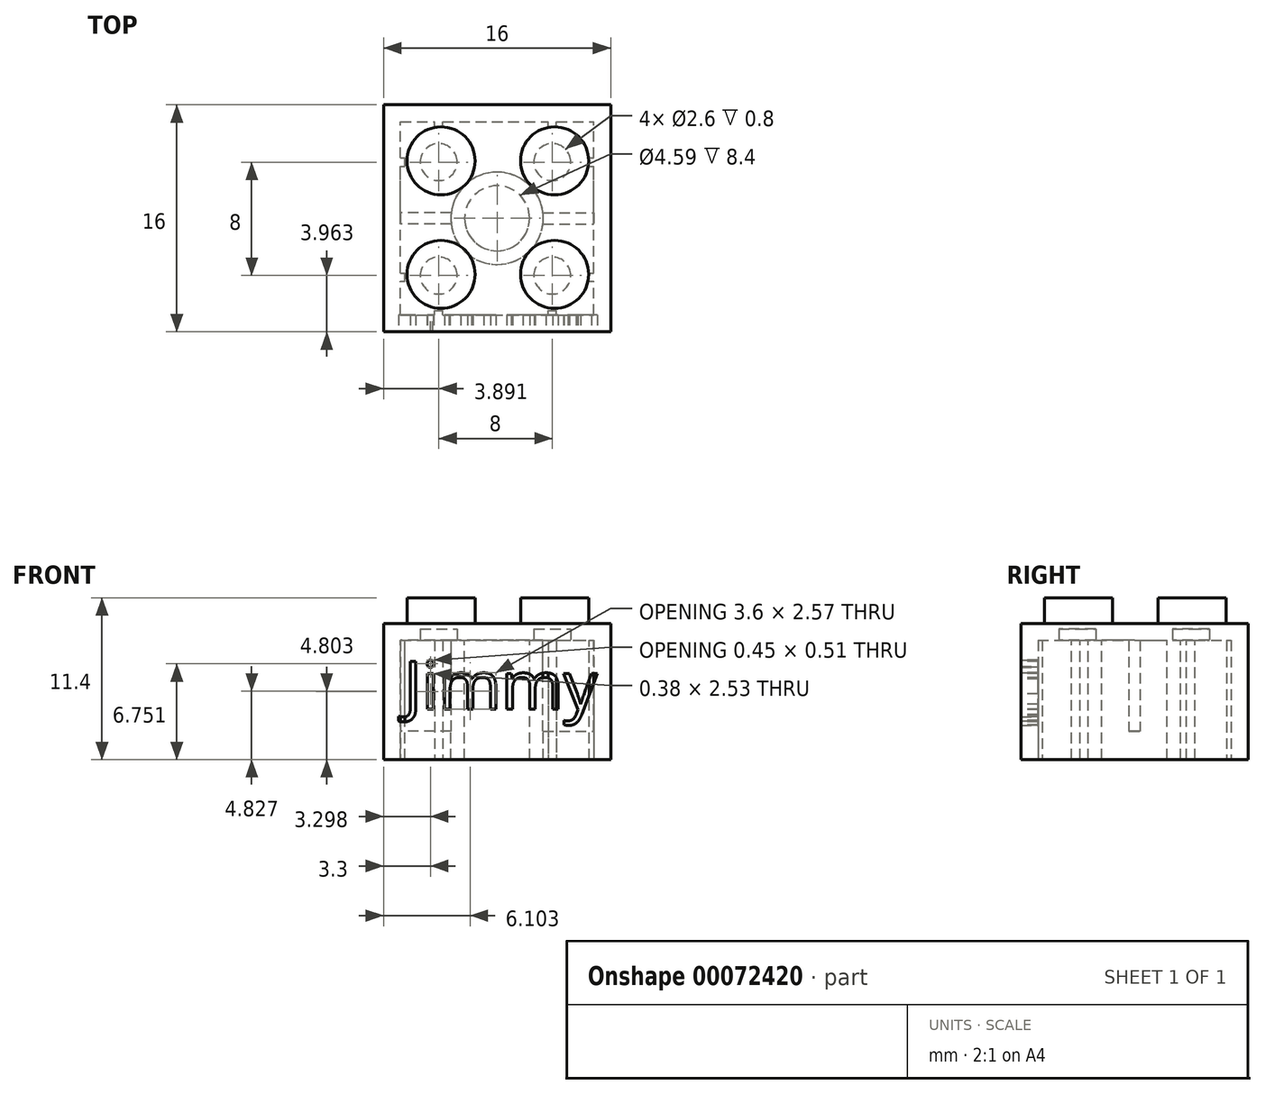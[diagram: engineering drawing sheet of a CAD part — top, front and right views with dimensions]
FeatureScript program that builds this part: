
annotation { "Feature Type Name" : "Feature", "Feature Type Description" : "" }
export const myFeature = defineFeature(function(context is Context, id is Id, definition is map)
    precondition{}
    {
        {
            var Q0;
            Q0=qCreatedBy(makeId("Top.planeOp"),FACE);
            var sketch = newSketch(context, id + "F0", { "sketchPlane" : qUnion([Q0])});
            skLineSegment(sketch, "E0.rect.bottom", {"start": v(8, 8) * mm, "end": v(-8, 8) * mm});
            skLineSegment(sketch, "E0.rect.top", {"start": v(8, -8) * mm, "end": v(-8, -8) * mm});
            skLineSegment(sketch, "E0.rect.left", {"start": v(8, 8) * mm, "end": v(8, -8) * mm});
            skLineSegment(sketch, "E0.rect.right", {"start": v(-8, 8) * mm, "end": v(-8, -8) * mm});
            skPoint(sketch, "E0.rect.middle", {"position": v(0, 0) * mm});
            skSolve(sketch);
        }
        {
            var Q0;
            Q0 = qSketchRegion(id + "F0", true);
            var Q1;
            Q1=makeQuery(id+"F0.imprint","IMPRINT",FACE,{"disambiguationData":[TD([[makeQuery(id+"F0.imprint","IMPRINT",EDGE,{"derivedFrom":sQuery(id+"F0.wireOp",EDGE,"E0.rect.bottom")}),1.0]])]});
            extrude(context, id + "F1", {"entities" : qUnion([Q0, Q1]), "depth" : 9.6 * mm});
        }
        {
            var Q0;
            Q0=makeQuery(id+"F1.opExtrude","CAP_FACE",FACE,{"disambiguationData":[OSD([sQuery(id+"F0.wireOp",EDGE,"E0.rect.bottom"),sQuery(id+"F0.wireOp",EDGE,"E0.rect.top"),sQuery(id+"F0.wireOp",EDGE,"E0.rect.left"),sQuery(id+"F0.wireOp",EDGE,"E0.rect.right")])],"isStart":true});
            var sketch = newSketch(context, id + "F2", { "sketchPlane" : qUnion([Q0])});
            skLineSegment(sketch, "E1.rect.bottom", {"start": v(6.8, 6.8) * mm, "end": v(-6.8, 6.8) * mm});
            skLineSegment(sketch, "E1.rect.top", {"start": v(6.8, -6.8) * mm, "end": v(-6.8, -6.8) * mm});
            skLineSegment(sketch, "E1.rect.left", {"start": v(6.8, 6.8) * mm, "end": v(6.8, -6.8) * mm});
            skLineSegment(sketch, "E1.rect.right", {"start": v(-6.8, 6.8) * mm, "end": v(-6.8, -6.8) * mm});
            skPoint(sketch, "E1.rect.middle", {"position": v(0, 0) * mm});
            skSolve(sketch);
        }
        {
            var Q0;
            Q0 = qSketchRegion(id + "F2", true);
            var Q1;
            Q1=makeQuery(id+"F2.imprint","IMPRINT",FACE,{"disambiguationData":[TD([[makeQuery(id+"F2.imprint","IMPRINT",EDGE,{"derivedFrom":sQuery(id+"F2.wireOp",EDGE,"E1.rect.bottom")}),1.0]])]});
            extrude(context, id + "F3", {"entities" : qUnion([Q0, Q1]), "operationType" : NewBodyOperationType.REMOVE, "oppositeDirection" : true, "depth" : 8.4 * mm});
        }
        {
            var Q0;
            Q0=makeQuery(id+"F3.boolean.opBoolean","COPY",FACE,{"derivedFrom":makeQuery(id+"F3.opExtrude","CAP_FACE",FACE,{"disambiguationData":[OSD([sQuery(id+"F2.wireOp",EDGE,"E1.rect.bottom"),sQuery(id+"F2.wireOp",EDGE,"E1.rect.top"),sQuery(id+"F2.wireOp",EDGE,"E1.rect.left"),sQuery(id+"F2.wireOp",EDGE,"E1.rect.right")])],"isStart":false})});
            var sketch = newSketch(context, id + "F4", { "sketchPlane" : qUnion([Q0])});
            skCircle(sketch, "E2", {"center": v(-4.1, 4.04) * mm, "radius": 1.3 * mm});
            skCircle(sketch, "E3.0.1.0", {"center": v(-4.1, -3.96) * mm, "radius": 1.3 * mm});
            skCircle(sketch, "E3.1.0.0", {"center": v(3.9, 4.04) * mm, "radius": 1.3 * mm});
            skCircle(sketch, "E3.1.1.0", {"center": v(3.9, -3.96) * mm, "radius": 1.3 * mm});
            skLineSegment(sketch, "E3.direction1", {"start": v(-4.1, 4.04) * mm, "end": v(3.9, 4.04) * mm, "construction": true});
            skLineSegment(sketch, "E3.direction2", {"start": v(-4.1, 4.04) * mm, "end": v(-4.1, -3.96) * mm, "construction": true});
            skSolve(sketch);
        }
        {
            var Q0;
            Q0=makeQuery(id+"F1.opExtrude","CAP_FACE",FACE,{"disambiguationData":[OSD([sQuery(id+"F0.wireOp",EDGE,"E0.rect.bottom"),sQuery(id+"F0.wireOp",EDGE,"E0.rect.top"),sQuery(id+"F0.wireOp",EDGE,"E0.rect.left"),sQuery(id+"F0.wireOp",EDGE,"E0.rect.right")])],"isStart":false});
            var sketch = newSketch(context, id + "F5", { "sketchPlane" : qUnion([Q0])});
            skCircle(sketch, "E4", {"center": v(-3.95, 4.05) * mm, "radius": 2.4 * mm});
            skCircle(sketch, "E5.0.1.0", {"center": v(-3.95, -3.95) * mm, "radius": 2.4 * mm});
            skCircle(sketch, "E5.1.0.0", {"center": v(4.05, 4.05) * mm, "radius": 2.4 * mm});
            skCircle(sketch, "E5.1.1.0", {"center": v(4.05, -3.95) * mm, "radius": 2.4 * mm});
            skLineSegment(sketch, "E5.direction1", {"start": v(-3.95, 4.05) * mm, "end": v(4.05, 4.05) * mm, "construction": true});
            skLineSegment(sketch, "E5.direction2", {"start": v(-3.95, 4.05) * mm, "end": v(-3.95, -3.95) * mm, "construction": true});
            skSolve(sketch);
        }
        {
            var Q0;
            Q0 = qSketchRegion(id + "F5", true);
            extrude(context, id + "F6", {"entities" : qUnion([Q0]), "operationType" : NewBodyOperationType.ADD, "depth" : 1.8 * mm});
        }
        {
            var Q0;
            Q0=makeQuery(id+"F4.imprint","IMPRINT",FACE,{"disambiguationData":[TD([[makeQuery(id+"F4.imprint","IMPRINT",EDGE,{"derivedFrom":sQuery(id+"F4.wireOp",EDGE,"E2")}),-1.0]])]});
            var sketch = newSketch(context, id + "F7", { "sketchPlane" : qUnion([Q0])});
            skCircle(sketch, "E6", {"center": v(0, 0) * mm, "radius": 2.3 * mm});
            skCircle(sketch, "E7", {"center": v(0, 0) * mm, "radius": 3.25 * mm});
            skSolve(sketch);
        }
        {
            var Q0;
            Q0 = qSketchRegion(id + "F7", true);
            var Q1;
            Q1=makeQuery(id+"F1.opExtrude","CAP_FACE",FACE,{"disambiguationData":[OSD([sQuery(id+"F0.wireOp",EDGE,"E0.rect.bottom"),sQuery(id+"F0.wireOp",EDGE,"E0.rect.top"),sQuery(id+"F0.wireOp",EDGE,"E0.rect.left"),sQuery(id+"F0.wireOp",EDGE,"E0.rect.right")])],"isStart":true});
            extrude(context, id + "F8", {"entities" : qUnion([Q0]), "operationType" : NewBodyOperationType.ADD, "endBound" : BoundingType.UP_TO_SURFACE, "endBoundEntityFace" : qUnion([Q1]), "depth" : 25 * mm});
        }
        {
            var Q0;
            Q0=qCreatedBy(makeId("Top.planeOp"),FACE);
            var sketch = newSketch(context, id + "F9", { "sketchPlane" : qUnion([Q0])});
            skLineSegment(sketch, "E8.bottom", {"start": v(-4.41, -6.8) * mm, "end": v(-3.81, -6.8) * mm});
            skLineSegment(sketch, "E8.top", {"start": v(-4.41, -6.5) * mm, "end": v(-3.81, -6.5) * mm});
            skLineSegment(sketch, "E8.left", {"start": v(-4.41, -6.8) * mm, "end": v(-4.41, -6.5) * mm});
            skLineSegment(sketch, "E8.right", {"start": v(-3.81, -6.8) * mm, "end": v(-3.81, -6.5) * mm});
            skLineSegment(sketch, "E9.0.1.0", {"start": v(-4.41, 6.5) * mm, "end": v(-3.81, 6.5) * mm});
            skLineSegment(sketch, "E9.0.1.1", {"start": v(-3.81, 6.5) * mm, "end": v(-3.81, 6.8) * mm});
            skLineSegment(sketch, "E9.0.1.2", {"start": v(-4.41, 6.8) * mm, "end": v(-3.81, 6.8) * mm});
            skLineSegment(sketch, "E9.0.1.3", {"start": v(-4.41, 6.5) * mm, "end": v(-4.41, 6.8) * mm});
            skLineSegment(sketch, "E9.1.0.0", {"start": v(3.59, -6.8) * mm, "end": v(4.19, -6.8) * mm});
            skLineSegment(sketch, "E9.1.0.1", {"start": v(4.19, -6.8) * mm, "end": v(4.19, -6.5) * mm});
            skLineSegment(sketch, "E9.1.0.2", {"start": v(3.59, -6.5) * mm, "end": v(4.19, -6.5) * mm});
            skLineSegment(sketch, "E9.1.0.3", {"start": v(3.59, -6.8) * mm, "end": v(3.59, -6.5) * mm});
            skLineSegment(sketch, "E9.1.1.0", {"start": v(3.59, 6.5) * mm, "end": v(4.19, 6.5) * mm});
            skLineSegment(sketch, "E9.1.1.1", {"start": v(4.19, 6.5) * mm, "end": v(4.19, 6.8) * mm});
            skLineSegment(sketch, "E9.1.1.2", {"start": v(3.59, 6.8) * mm, "end": v(4.19, 6.8) * mm});
            skLineSegment(sketch, "E9.1.1.3", {"start": v(3.59, 6.5) * mm, "end": v(3.59, 6.8) * mm});
            skLineSegment(sketch, "E9.direction1", {"start": v(-4.41, -6.8) * mm, "end": v(3.59, -6.8) * mm, "construction": true});
            skSolve(sketch);
        }
        {
            var Q0;
            Q0=makeQuery(id+"F4.imprint","IMPRINT",FACE,{"disambiguationData":[TD([[makeQuery(id+"F4.imprint","IMPRINT",EDGE,{"derivedFrom":sQuery(id+"F4.wireOp",EDGE,"E2")}),-1.0]])]});
            var sketch = newSketch(context, id + "F10", { "sketchPlane" : qUnion([Q0])});
            skSolve(sketch);
        }
        {
            var Q0;
            Q0=makeQuery(id+"F4.imprint","IMPRINT",FACE,{"disambiguationData":[TD([[makeQuery(id+"F4.imprint","IMPRINT",EDGE,{"derivedFrom":sQuery(id+"F4.wireOp",EDGE,"E2")}),-1.0]])]});
            var sketch = newSketch(context, id + "F11", { "sketchPlane" : qUnion([Q0])});
            skSolve(sketch);
        }
        {
            var Q0;
            Q0 = qSketchRegion(id + "F4", true);
            extrude(context, id + "F12", {"entities" : qUnion([Q0]), "operationType" : NewBodyOperationType.REMOVE, "oppositeDirection" : true, "depth" : 0.8 * mm});
        }
        {
            var Q0;
            Q0=makeQuery(id+"F11.imprint","IMPRINT",FACE,{"disambiguationData":[TD([[makeQuery(id+"F11.imprint","IMPRINT",EDGE,{"derivedFrom":makeQuery(id+"F4.imprint","IMPRINT",EDGE,{"derivedFrom":sQuery(id+"F4.wireOp",EDGE,"E2")})}),-1.0]])]});
            var sketch = newSketch(context, id + "F13", { "sketchPlane" : qUnion([Q0])});
            skLineSegment(sketch, "E10.bottom", {"start": v(-6.8, -3.65) * mm, "end": v(-6.5, -3.65) * mm});
            skLineSegment(sketch, "E10.top", {"start": v(-6.8, -4.25) * mm, "end": v(-6.5, -4.25) * mm});
            skLineSegment(sketch, "E10.left", {"start": v(-6.8, -3.65) * mm, "end": v(-6.8, -4.25) * mm});
            skLineSegment(sketch, "E10.right", {"start": v(-6.5, -3.65) * mm, "end": v(-6.5, -4.25) * mm});
            skLineSegment(sketch, "E11.0.1.0", {"start": v(-6.8, 4.45) * mm, "end": v(-6.5, 4.45) * mm});
            skLineSegment(sketch, "E11.0.1.1", {"start": v(-6.5, 4.45) * mm, "end": v(-6.5, 3.85) * mm});
            skLineSegment(sketch, "E11.0.1.2", {"start": v(-6.8, 3.85) * mm, "end": v(-6.5, 3.85) * mm});
            skLineSegment(sketch, "E11.0.1.3", {"start": v(-6.8, 4.45) * mm, "end": v(-6.8, 3.85) * mm});
            skLineSegment(sketch, "E11.1.0.0", {"start": v(6.5, -3.65) * mm, "end": v(6.8, -3.65) * mm});
            skLineSegment(sketch, "E11.1.0.1", {"start": v(6.8, -3.65) * mm, "end": v(6.8, -4.25) * mm});
            skLineSegment(sketch, "E11.1.0.2", {"start": v(6.5, -4.25) * mm, "end": v(6.8, -4.25) * mm});
            skLineSegment(sketch, "E11.1.0.3", {"start": v(6.5, -3.65) * mm, "end": v(6.5, -4.25) * mm});
            skLineSegment(sketch, "E11.1.1.0", {"start": v(6.5, 4.45) * mm, "end": v(6.8, 4.45) * mm});
            skLineSegment(sketch, "E11.1.1.1", {"start": v(6.8, 4.45) * mm, "end": v(6.8, 3.85) * mm});
            skLineSegment(sketch, "E11.1.1.2", {"start": v(6.5, 3.85) * mm, "end": v(6.8, 3.85) * mm});
            skLineSegment(sketch, "E11.1.1.3", {"start": v(6.5, 4.45) * mm, "end": v(6.5, 3.85) * mm});
            skLineSegment(sketch, "E11.direction2", {"start": v(-6.8, -3.65) * mm, "end": v(-6.8, 4.45) * mm, "construction": true});
            skSolve(sketch);
        }
        {
            var Q0;
            Q0 = qSketchRegion(id + "F13", true);
            var Q1;
            Q1=makeQuery(id+"F1.opExtrude","CAP_FACE",FACE,{"disambiguationData":[OSD([sQuery(id+"F0.wireOp",EDGE,"E0.rect.bottom"),sQuery(id+"F0.wireOp",EDGE,"E0.rect.top"),sQuery(id+"F0.wireOp",EDGE,"E0.rect.left"),sQuery(id+"F0.wireOp",EDGE,"E0.rect.right")])],"isStart":true});
            extrude(context, id + "F14", {"entities" : qUnion([Q0]), "operationType" : NewBodyOperationType.ADD, "endBound" : BoundingType.UP_TO_SURFACE, "endBoundEntityFace" : qUnion([Q1]), "depth" : 25 * mm});
        }
        {
            var Q0;
            Q0 = qSketchRegion(id + "F9", true);
            extrude(context, id + "F15", {"entities" : qUnion([Q0]), "operationType" : NewBodyOperationType.ADD, "depth" : 8.4 * mm});
        }
        {
            var Q0;
            Q0=makeQuery(id+"F10.imprint","IMPRINT",FACE,{"disambiguationData":[TD([[makeQuery(id+"F10.imprint","IMPRINT",EDGE,{"derivedFrom":makeQuery(id+"F4.imprint","IMPRINT",EDGE,{"derivedFrom":sQuery(id+"F4.wireOp",EDGE,"E2")})}),-1.0]])]});
            var sketch = newSketch(context, id + "F16", { "sketchPlane" : qUnion([Q0])});
            skLineSegment(sketch, "E12.bottom", {"start": v(-3, 0.4) * mm, "end": v(-7.11, 0.4) * mm});
            skLineSegment(sketch, "E12.top", {"start": v(-3, -0.4) * mm, "end": v(-7.11, -0.4) * mm});
            skLineSegment(sketch, "E12.left", {"start": v(-3, 0.4) * mm, "end": v(-3, -0.4) * mm});
            skLineSegment(sketch, "E12.right", {"start": v(-7.11, 0.4) * mm, "end": v(-7.11, -0.4) * mm});
            skLineSegment(sketch, "E13.bottom", {"start": v(2.75, 0.4) * mm, "end": v(7.1, 0.4) * mm});
            skLineSegment(sketch, "E13.top", {"start": v(2.75, -0.4) * mm, "end": v(7.1, -0.4) * mm});
            skLineSegment(sketch, "E13.left", {"start": v(2.75, 0.4) * mm, "end": v(2.75, -0.4) * mm});
            skLineSegment(sketch, "E13.right", {"start": v(7.1, 0.4) * mm, "end": v(7.1, -0.4) * mm});
            skSolve(sketch);
        }
        {
            var Q0;
            Q0 = qSketchRegion(id + "F16", true);
            extrude(context, id + "F17", {"entities" : qUnion([Q0]), "operationType" : NewBodyOperationType.ADD, "depth" : 6.4 * mm});
        }
        {
            var Q0;
            Q0=makeQuery(id+"F1.opExtrude","SWEPT_FACE",FACE,{"disambiguationData":[OSD([sQuery(id+"F0.wireOp",EDGE,"E0.rect.top")])]});
            var sketch = newSketch(context, id + "F18", { "sketchPlane" : qUnion([Q0])});
            skText(sketch, "E14", { "text": "Jimmy \n", "fontName": "OpenSans-Regular.ttf"});
            const initialGuessF18  = {"E14": [-0.00656, 0.00354, 1, 0, 0.0034]};
            skSetInitialGuess(sketch, initialGuessF18);
            skSolve(sketch);
        }
        {
            var Q0;
            Q0 = qSketchRegion(id + "F18", true);
            extrude(context, id + "F19", {"entities" : qUnion([Q0]), "operationType" : NewBodyOperationType.REMOVE, "oppositeDirection" : true, "depth" : 1.2 * mm});
        }
    });
